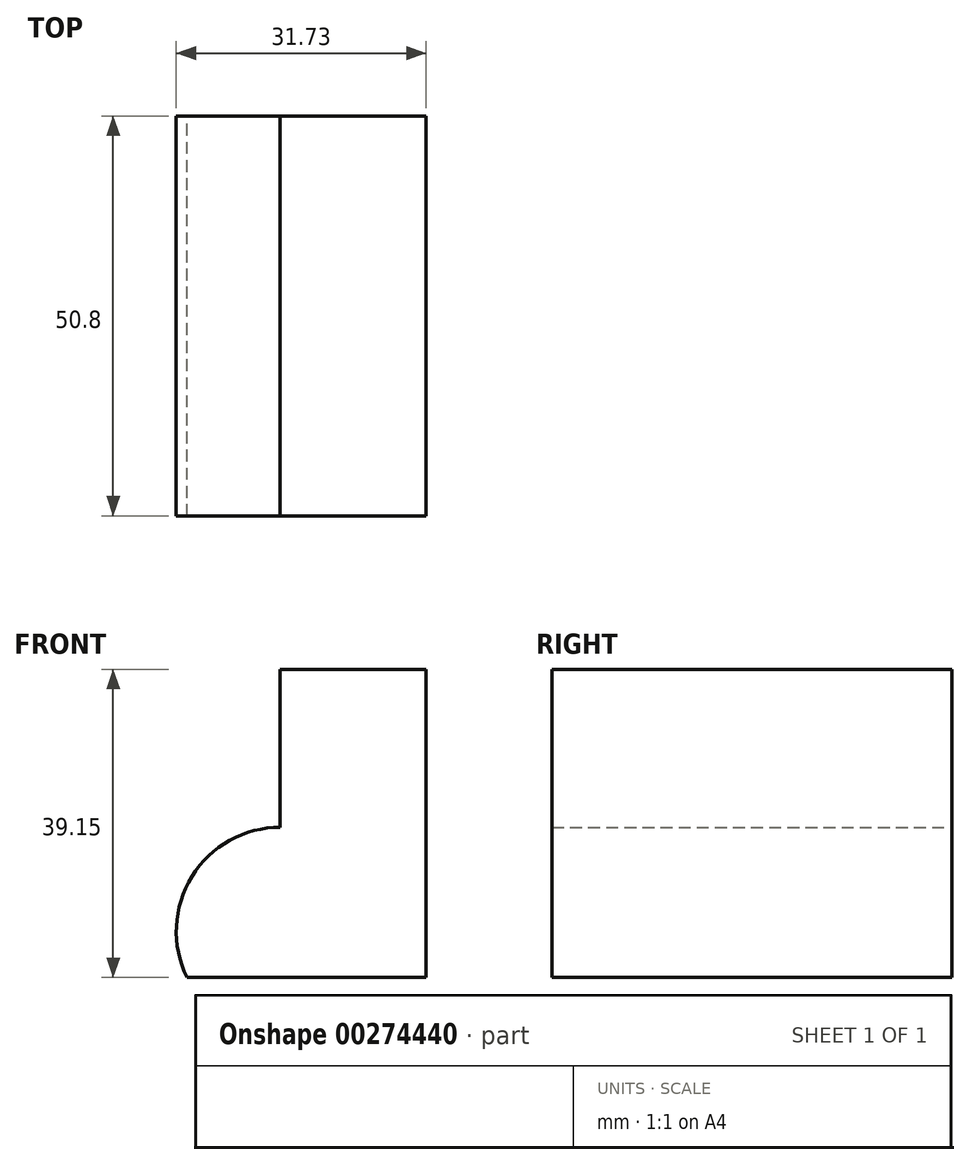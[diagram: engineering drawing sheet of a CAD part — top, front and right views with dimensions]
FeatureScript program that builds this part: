
annotation { "Feature Type Name" : "Feature", "Feature Type Description" : "" }
export const myFeature = defineFeature(function(context is Context, id is Id, definition is map)
    precondition{}
    {
        {
            var Q0;
            Q0=qCreatedBy(makeId("Front.planeOp"),FACE);
            var sketch = newSketch(context, id + "F0", { "sketchPlane" : qUnion([Q0])});
            skLineSegment(sketch, "E0", {"start": v(0, 0) * mm, "end": v(0, 39.15) * mm});
            skLineSegment(sketch, "E1", {"start": v(0, 0) * mm, "end": v(-30.36, 0) * mm});
            skLineSegment(sketch, "E2", {"start": v(0, 39.15) * mm, "end": v(-18.52, 39.15) * mm});
            skLineSegment(sketch, "E3", {"start": v(-18.52, 39.15) * mm, "end": v(-18.52, 19.1) * mm});
            skArc(sketch, "E4", {"start": v(-18.52, 19.1) * mm, "mid": v(-29.74, 12.83) * mm, "end": v(-30.36, 0) * mm});
            skSolve(sketch);
        }
        {
            var Q0;
            Q0 = qSketchRegion(id + "F0", true);
            extrude(context, id + "F1", {"entities" : qUnion([Q0]), "depth" : 50.8 * mm});
        }
    });
